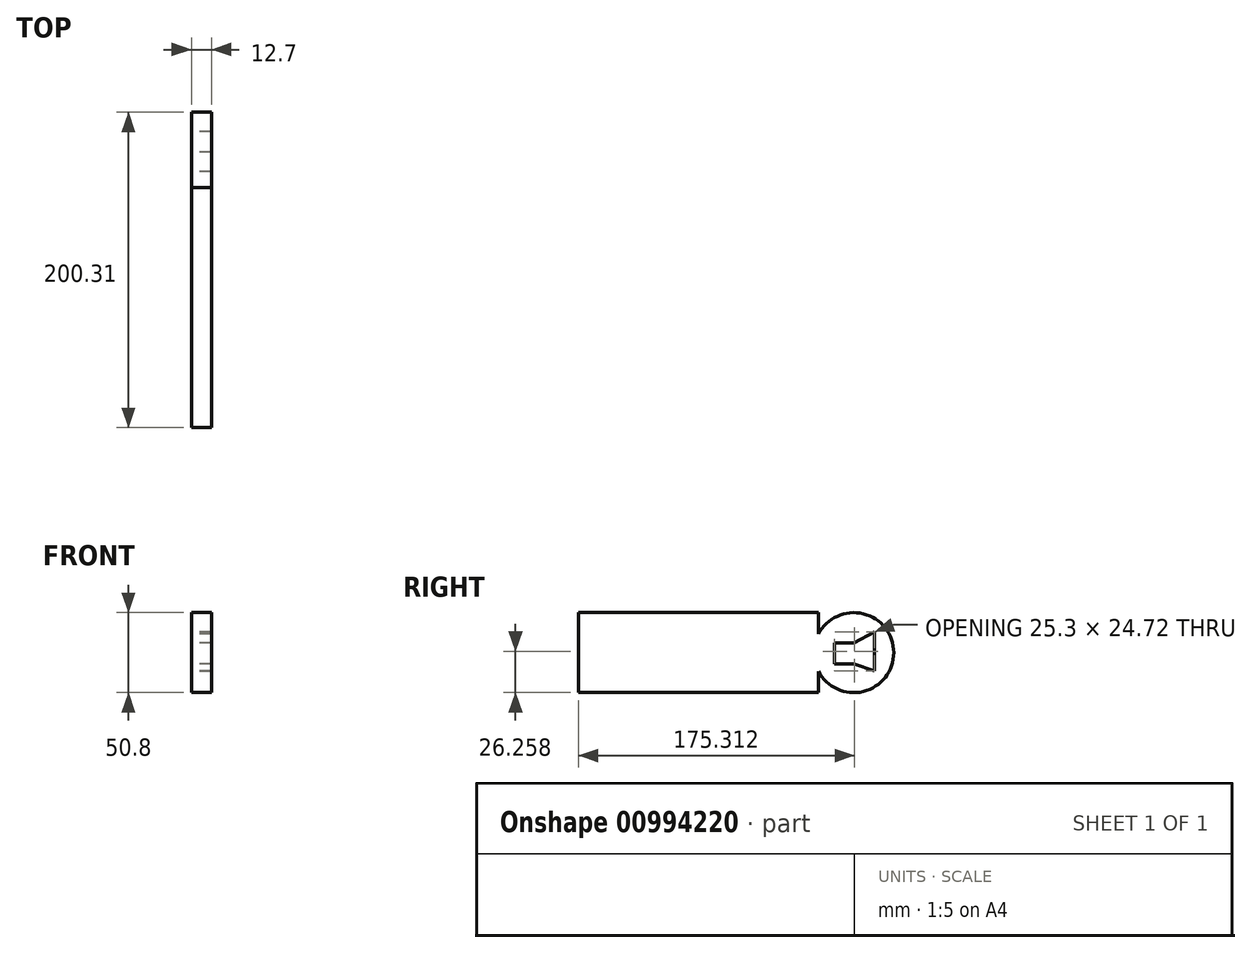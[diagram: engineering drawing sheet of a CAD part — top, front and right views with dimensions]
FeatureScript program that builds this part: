
annotation { "Feature Type Name" : "Feature", "Feature Type Description" : "" }
export const myFeature = defineFeature(function(context is Context, id is Id, definition is map)
    precondition{}
    {
        {
            var Q0;
            Q0=qCreatedBy(makeId("Right.planeOp"),FACE);
            var sketch = newSketch(context, id + "F0", { "sketchPlane" : qUnion([Q0])});
            skLineSegment(sketch, "E0.bottom", {"start": v(-22.51, 25.4) * mm, "end": v(-174.91, 25.4) * mm});
            skLineSegment(sketch, "E0.top", {"start": v(-22.51, -25.4) * mm, "end": v(-174.91, -25.4) * mm});
            skLineSegment(sketch, "E0.left", {"start": v(-22.51, 25.4) * mm, "end": v(-22.51, 11.76) * mm});
            skLineSegment(sketch, "E0.right", {"start": v(-174.91, 25.4) * mm, "end": v(-174.91, -25.4) * mm});
            skPoint(sketch, "E0.middle", {"position": v(-98.71, 0) * mm});
            skArc(sketch, "E1", {"start": v(-22.51, -11.76) * mm, "mid": v(25.4, 0) * mm, "end": v(-22.51, 11.76) * mm});
            skLineSegment(sketch, "E2.trimOffspring", {"start": v(-22.51, -11.76) * mm, "end": v(-22.51, -25.4) * mm});
            skPoint(sketch, "E3.centerSnap0", {"position": v(-174.91, 0) * mm});
            skPoint(sketch, "E3.center.orphan", {"position": v(-3.9, 0) * mm});
            skLineSegment(sketch, "E4", {"start": v(-12.25, 6.2) * mm, "end": v(0, 6.2) * mm});
            skLineSegment(sketch, "E5", {"start": v(0, 6.2) * mm, "end": v(13.05, 13.22) * mm});
            skLineSegment(sketch, "E6", {"start": v(13.05, 13.22) * mm, "end": v(13.05, -11.5) * mm});
            skLineSegment(sketch, "E7", {"start": v(13.05, -11.5) * mm, "end": v(0, -7.07) * mm});
            skLineSegment(sketch, "E8", {"start": v(0, -7.07) * mm, "end": v(-12.25, -7.07) * mm});
            skLineSegment(sketch, "E9", {"start": v(-12.25, -7.07) * mm, "end": v(-12.25, 6.2) * mm});
            skSolve(sketch);
        }
        {
            var Q0;
            Q0=makeQuery(id+"F0.imprint","IMPRINT",FACE,{"disambiguationData":[TD([[makeQuery(id+"F0.imprint","IMPRINT",EDGE,{"derivedFrom":sQuery(id+"F0.wireOp",EDGE,"E0.bottom")}),1.0]])]});
            extrude(context, id + "F1", {"entities" : qUnion([Q0]), "depth" : 12.7 * mm, "offsetDistance" : 25.4 * mm});
        }
        {
            var Q0;
            Q0=makeQuery(id+"F1.opExtrude","CAP_FACE",FACE,{"disambiguationData":[OSD([sQuery(id+"F0.wireOp",EDGE,"E0.bottom"),sQuery(id+"F0.wireOp",EDGE,"E0.top"),sQuery(id+"F0.wireOp",EDGE,"E0.left"),sQuery(id+"F0.wireOp",EDGE,"E0.right"),sQuery(id+"F0.wireOp",EDGE,"E1"),sQuery(id+"F0.wireOp",EDGE,"E2.trimOffspring"),sQuery(id+"F0.wireOp",EDGE,"E4"),sQuery(id+"F0.wireOp",EDGE,"E5"),sQuery(id+"F0.wireOp",EDGE,"E6"),sQuery(id+"F0.wireOp",EDGE,"E7"),sQuery(id+"F0.wireOp",EDGE,"E8"),sQuery(id+"F0.wireOp",EDGE,"E9")])],"isStart":true});
            var sketch = newSketch(context, id + "F2", { "sketchPlane" : qUnion([Q0])});
            skText(sketch, "E10", { "text": "Demi\n", "fontName": "OpenSans-Bold.ttf"});
            const initialGuessF2  = {"E10": [0.03455, -0.01035, 1, 0, 0.0234]};
            skSetInitialGuess(sketch, initialGuessF2);
            skSolve(sketch);
        }
        {
            var Q0;
            Q0=makeQuery(id+"F2.imprint","IMPRINT",FACE,{"disambiguationData":[TD([[makeQuery(id+"F2.imprint","IMPRINT",EDGE,{"derivedFrom":sQuery(id+"F2.wireOp",EDGE,"E10.sketch_text.stroke-0")}),-1.0]])]});
            var Q1;
            Q1=makeQuery(id+"F2.imprint","IMPRINT",FACE,{"disambiguationData":[TD([[makeQuery(id+"F2.imprint","IMPRINT",EDGE,{"derivedFrom":sQuery(id+"F2.wireOp",EDGE,"E10.sketch_text.stroke-12")}),-1.0]])]});
            var Q2;
            Q2=makeQuery(id+"F2.imprint","IMPRINT",FACE,{"disambiguationData":[TD([[makeQuery(id+"F2.imprint","IMPRINT",EDGE,{"derivedFrom":sQuery(id+"F2.wireOp",EDGE,"E10.sketch_text.stroke-32")}),-1.0]])]});
            var Q3;
            Q3=makeQuery(id+"F2.imprint","IMPRINT",FACE,{"disambiguationData":[TD([[makeQuery(id+"F2.imprint","IMPRINT",EDGE,{"derivedFrom":sQuery(id+"F2.wireOp",EDGE,"E10.sketch_text.stroke-65")}),-1.0]])]});
            var Q4;
            Q4=makeQuery(id+"F2.imprint","IMPRINT",FACE,{"disambiguationData":[TD([[makeQuery(id+"F2.imprint","IMPRINT",EDGE,{"derivedFrom":sQuery(id+"F2.wireOp",EDGE,"E10.sketch_text.stroke-60")}),-1.0]])]});
            var Q5;
            Q5 = qConstructionFilter(qBodyType(qCreatedBy(id + "F2" ,EDGE), BodyType.WIRE), ConstructionObject.NO);
            extrude(context, id + "F3", {"entities" : qUnion([Q0, Q1, Q2, Q3, Q4]), "bodyType" : ToolBodyType.SURFACE, "surfaceEntities" : qUnion([Q5]), "depth" : 25.4 * mm, "offsetDistance" : 25.4 * mm});
        }
    });
